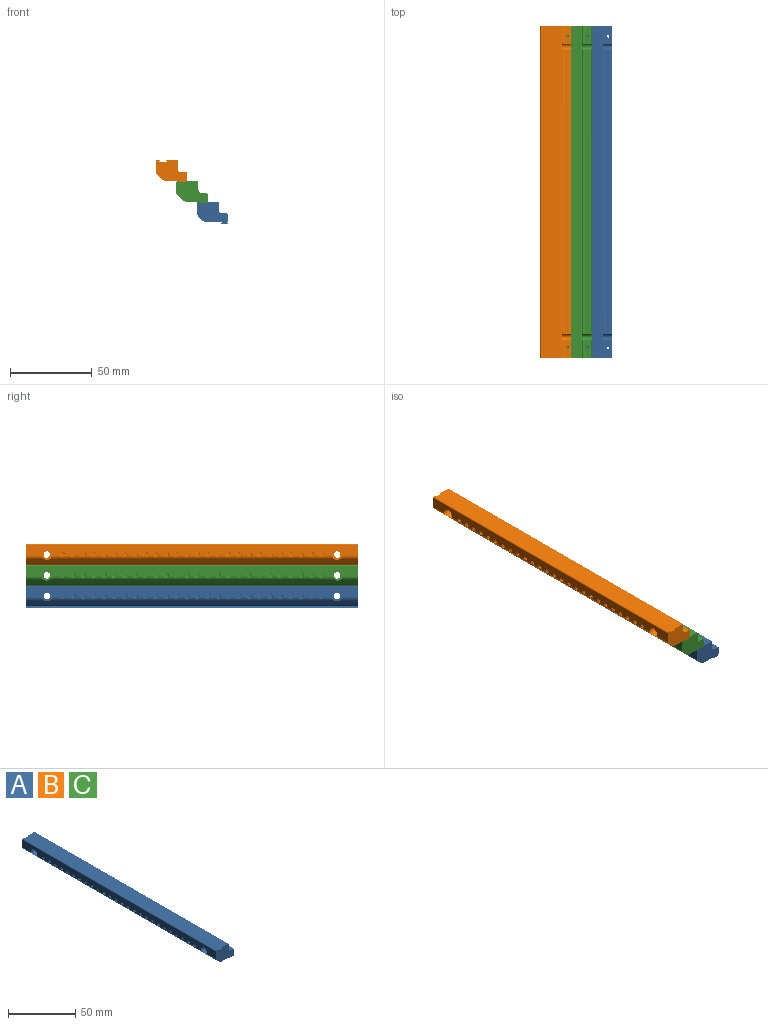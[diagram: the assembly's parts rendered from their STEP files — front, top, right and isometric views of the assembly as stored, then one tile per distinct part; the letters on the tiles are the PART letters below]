
ASSEMBLY  parts=3 mates=2
PART A: 227 faces, bbox 19.7x203.4x14 mm
  f0: cylinder r=3.17mm len=174.07mm, axis (0,-1,0), area 346.1mm2, adj f2,f39,f67,f69,f73,f74,f75,f79
  f1: plane 3.26x3.25mm, normal (-1,0,0), area 7.3mm2, adj f221,f222,f223,f226
  f2: plane 203.42x7.57mm, normal (-1,0,0), area 1082.2mm2, adj f0,f28,f38,f56,f57,f58,f67,f69
  f3: plane 3.26x3.25mm, normal (-1,0,0), area 7.3mm2, adj f215,f216,f217,f220
  f4: plane 3.26x3.25mm, normal (-1,0,0), area 7.3mm2, adj f209,f210,f211,f214
  f5: plane 3.26x3.25mm, normal (-1,0,0), area 7.3mm2, adj f203,f204,f205,f208
  f6: plane 3.26x3.25mm, normal (-1,0,0), area 7.3mm2, adj f197,f198,f199,f202
  f7: plane 3.26x3.25mm, normal (-1,0,0), area 7.3mm2, adj f191,f192,f193,f196
  f8: plane 3.26x3.25mm, normal (-1,0,0), area 7.3mm2, adj f185,f186,f187,f190
  f9: plane 3.26x3.25mm, normal (-1,0,0), area 7.3mm2, adj f179,f180,f181,f184
  f10: plane 3.26x3.25mm, normal (-1,0,0), area 7.3mm2, adj f173,f174,f175,f178
  f11: plane 3.26x3.25mm, normal (-1,0,0), area 7.3mm2, adj f167,f168,f169,f172
  f12: plane 3.26x3.25mm, normal (-1,0,0), area 7.3mm2, adj f161,f162,f163,f166
  f13: plane 3.26x3.25mm, normal (-1,0,0), area 7.3mm2, adj f155,f156,f157,f160
  f14: plane 3.26x3.25mm, normal (-1,0,0), area 7.3mm2, adj f149,f150,f151,f154
  f15: plane 3.26x3.25mm, normal (-1,0,0), area 7.3mm2, adj f143,f144,f145,f148
  f16: plane 3.26x3.25mm, normal (-1,0,0), area 7.3mm2, adj f137,f138,f139,f142
  f17: plane 3.26x3.25mm, normal (-1,0,0), area 7.3mm2, adj f131,f132,f133,f136
  f18: plane 3.26x3.25mm, normal (-1,0,0), area 7.3mm2, adj f125,f126,f127,f130
  f19: plane 3.26x3.25mm, normal (-1,0,0), area 7.3mm2, adj f119,f120,f121,f124
  f20: plane 3.26x3.25mm, normal (-1,0,0), area 7.3mm2, adj f113,f114,f115,f118
  f21: plane 3.26x3.25mm, normal (-1,0,0), area 7.3mm2, adj f107,f108,f109,f112
  f22: plane 3.26x3.25mm, normal (-1,0,0), area 7.3mm2, adj f101,f102,f103,f106
  f23: plane 3.26x3.25mm, normal (-1,0,0), area 7.3mm2, adj f95,f96,f97,f100
  f24: plane 3.26x3.25mm, normal (-1,0,0), area 7.3mm2, adj f89,f90,f91,f94
  f25: plane 3.26x3.25mm, normal (-1,0,0), area 7.3mm2, adj f83,f84,f85,f88
  f26: plane 3.26x3.25mm, normal (-1,0,0), area 7.3mm2, adj f77,f78,f79,f82
  f27: plane 3.26x3.25mm, normal (-1,0,0), area 7.3mm2, adj f71,f72,f73,f76
  f28: cylinder r=3.17mm len=10.84mm, axis (0,-1,0), area 24.9mm2, adj f2,f39,f58,f69
  f29: cylinder r=2.02mm len=14.22mm, axis (-1,0,0), area 136.6mm2, adj f31,f32,f33,f34,f35,f36,f46,f49
  f30: cylinder r=2.02mm len=14.22mm, axis (-1,0,0), area 136.6mm2, adj f31,f33,f35,f37,f46,f47,f48,f49
  f31: plane 174.12x3.18mm, normal (0,0,1), area 552.8mm2, adj f29,f30,f33,f35
  f32: plane 11x3.32mm, normal (0,0,1), area 32.1mm2, adj f29,f34,f36,f58,f63,f64,f65,f66
  f33: cylinder r=0.79mm len=175.39mm, axis (0,-1,0), area 217.6mm2, adj f29,f30,f31,f46
  f34: cylinder r=0.79mm len=11.5mm, axis (0,-1,0), area 13.8mm2, adj f29,f32,f46,f58
  f35: cylinder r=1.59mm len=174.12mm, axis (0,-1,0), area 434.1mm2, adj f29,f30,f31,f49
  f36: cylinder r=1.59mm len=10.86mm, axis (0,-1,0), area 27mm2, adj f29,f32,f49,f58
  f37: plane 11x3.32mm, normal (0,0,1), area 32.1mm2, adj f30,f47,f48,f57,f59,f60,f61,f62
  f38: cylinder r=3.17mm len=10.84mm, axis (0,-1,0), area 24.9mm2, adj f2,f39,f57,f67
  f39: plane 203.2x2.71mm, normal (-0.7,0,-0.71), area 771.8mm2, adj f0,f28,f38,f40,f57,f58,f67,f69
  f40: cylinder r=3.17mm len=203.2mm, axis (0,-1,0), area 504.1mm2, adj f39,f41,f57,f58
  f41: plane 203.2x9.24mm, normal (0,0,-1), area 1878.3mm2, adj f40,f42,f57,f58
  f42: plane 203.2x0.84mm, normal (-0.71,0,0.71), area 241.9mm2, adj f41,f43,f57,f58
  f43: plane 203.34x4.91mm, normal (0,0,-1), area 963mm2, adj f42,f44,f57,f58,f59,f60,f61,f62
  f44: plane 203.2x0.84mm, normal (0.71,0,0.71), area 241.9mm2, adj f43,f45,f57,f58
  f45: plane 203.2x0.84mm, normal (0,0,-1), area 171.1mm2, adj f44,f46,f57,f58
  f46: plane 203.2x4.71mm, normal (1,0,0), area 956.7mm2, adj f29,f30,f33,f34,f45,f47,f57,f58
  f47: cylinder r=0.79mm len=11.5mm, axis (0,-1,0), area 13.8mm2, adj f30,f37,f46,f57
  f48: cylinder r=1.59mm len=10.86mm, axis (0,-1,0), area 27mm2, adj f30,f37,f49,f57
  f49: plane 203.2x4.81mm, normal (1,0,0), area 970.7mm2, adj f29,f30,f35,f36,f48,f50,f57,f58
  f50: cylinder r=0.79mm len=203.2mm, axis (0,-1,0), area 253.4mm2, adj f49,f51,f57,f58
  f51: plane 203.2x7.01mm, normal (0,0,1), area 1424mm2, adj f50,f52,f57,f58
  f52: plane 203.2x0.84mm, normal (-0.71,0,-0.71), area 241.9mm2, adj f51,f53,f57,f58
  f53: plane 203.2x4.76mm, normal (0,0,1), area 967.7mm2, adj f52,f54,f57,f58
  f54: plane 203.2x0.84mm, normal (0.71,0,-0.71), area 241.9mm2, adj f53,f55,f57,f58
  f55: plane 203.2x1.82mm, normal (0,0,1), area 369.8mm2, adj f54,f56,f57,f58
  f56: cylinder r=0.79mm len=203.2mm, axis (0,-1,0), area 253.4mm2, adj f2,f55,f57,f58
  f57: plane 19.05x13.54mm, normal (0,1,0), area 191.3mm2, adj f2,f37,f38,f39,f40,f41,f42,f43
  f58: plane 19.05x13.54mm, normal (0,-1,0), area 191.3mm2, adj f2,f28,f32,f34,f36,f39,f40,f41
  f59: bspline ~6.78x2.35mm, area 22mm2, adj f37,f43,f61,f62
  f60: bspline ~6.78x2.35mm, area 21.9mm2, adj f37,f43,f61,f62
  f61: bspline ~6.59x2.41mm, area 6mm2, adj f37,f43,f59,f60
  f62: cylinder r=0.73mm len=6.35mm, axis (0,0,1), area 5.1mm2, adj f37,f43,f59,f60
  f63: bspline ~6.78x2.35mm, area 22mm2, adj f32,f43,f65,f66
  f64: bspline ~6.78x2.35mm, area 21.9mm2, adj f32,f43,f65,f66
  f65: bspline ~6.59x2.41mm, area 6mm2, adj f32,f43,f63,f64
  f66: cylinder r=0.73mm len=6.35mm, axis (0,0,1), area 5.1mm2, adj f32,f43,f63,f64
  f67: cylinder r=3.3mm len=6.6mm, axis (-1,0,0), area 93mm2, adj f0,f2,f38,f39,f68
  f68: plane 6.6x6.6mm, normal (-1,0,0), area 21.4mm2, adj f30,f67
  f69: cylinder r=3.3mm len=6.6mm, axis (-1,0,0), area 93mm2, adj f0,f2,f28,f39,f70
  f70: plane 6.6x6.6mm, normal (-1,0,0), area 21.4mm2, adj f29,f69
  f71: bspline ~10.17x4.06mm, area 58.1mm2, adj f2,f27,f73,f76
  f72: bspline ~10.17x4.06mm, area 57.8mm2, adj f2,f27,f73,f76
  f73: bspline ~9.89x4.15mm, area 15.3mm2, adj f0,f2,f27,f71,f72,f74,f75
  f74: cylinder r=1.78mm len=2.56mm, axis (-1,0,0), area 0mm2, adj f0,f2,f73
  f75: cylinder r=1.78mm len=2.63mm, axis (-1,0,0), area 0.2mm2, adj f0,f2,f73
  f76: cylinder r=1.33mm len=9.53mm, axis (-1,0,0), area 13.8mm2, adj f2,f27,f71,f72
  f77: bspline ~10.17x4.06mm, area 58.1mm2, adj f2,f26,f79,f82
  f78: bspline ~10.17x4.06mm, area 57.8mm2, adj f2,f26,f79,f82
  f79: bspline ~9.89x4.15mm, area 15.3mm2, adj f0,f2,f26,f77,f78,f80,f81
  f80: cylinder r=1.78mm len=2.56mm, axis (-1,0,0), area 0mm2, adj f0,f2,f79
  f81: cylinder r=1.78mm len=2.63mm, axis (-1,0,0), area 0.2mm2, adj f0,f2,f79
  f82: cylinder r=1.33mm len=9.53mm, axis (-1,0,0), area 13.8mm2, adj f2,f26,f77,f78
  f83: bspline ~10.17x4.06mm, area 58.1mm2, adj f2,f25,f85,f88
  f84: bspline ~10.17x4.06mm, area 57.8mm2, adj f2,f25,f85,f88
  f85: bspline ~9.89x4.15mm, area 15.3mm2, adj f0,f2,f25,f83,f84,f86,f87
  f86: cylinder r=1.78mm len=2.56mm, axis (-1,0,0), area 0mm2, adj f0,f2,f85
  f87: cylinder r=1.78mm len=2.63mm, axis (-1,0,0), area 0.2mm2, adj f0,f2,f85
  f88: cylinder r=1.33mm len=9.53mm, axis (-1,0,0), area 13.8mm2, adj f2,f25,f83,f84
  f89: bspline ~10.17x4.06mm, area 58.1mm2, adj f2,f24,f91,f94
  f90: bspline ~10.17x4.06mm, area 57.8mm2, adj f2,f24,f91,f94
  f91: bspline ~9.89x4.15mm, area 15.3mm2, adj f0,f2,f24,f89,f90,f92,f93
  f92: cylinder r=1.78mm len=2.56mm, axis (-1,0,0), area 0mm2, adj f0,f2,f91
  f93: cylinder r=1.78mm len=2.63mm, axis (-1,0,0), area 0.2mm2, adj f0,f2,f91
  f94: cylinder r=1.33mm len=9.53mm, axis (-1,0,0), area 13.8mm2, adj f2,f24,f89,f90
  f95: bspline ~10.17x4.06mm, area 58.1mm2, adj f2,f23,f97,f100
  f96: bspline ~10.17x4.06mm, area 57.8mm2, adj f2,f23,f97,f100
  f97: bspline ~9.89x4.15mm, area 15.3mm2, adj f0,f2,f23,f95,f96,f98,f99
  f98: cylinder r=1.78mm len=2.56mm, axis (-1,0,0), area 0mm2, adj f0,f2,f97
  f99: cylinder r=1.78mm len=2.63mm, axis (-1,0,0), area 0.2mm2, adj f0,f2,f97
  f100: cylinder r=1.33mm len=9.53mm, axis (-1,0,0), area 13.8mm2, adj f2,f23,f95,f96
  f101: bspline ~10.17x4.06mm, area 58.1mm2, adj f2,f22,f103,f106
  f102: bspline ~10.17x4.06mm, area 57.8mm2, adj f2,f22,f103,f106
  f103: bspline ~9.89x4.15mm, area 15.3mm2, adj f0,f2,f22,f101,f102,f104,f105
  f104: cylinder r=1.78mm len=2.56mm, axis (-1,0,0), area 0mm2, adj f0,f2,f103
  f105: cylinder r=1.78mm len=2.63mm, axis (-1,0,0), area 0.2mm2, adj f0,f2,f103
  f106: cylinder r=1.33mm len=9.53mm, axis (-1,0,0), area 13.8mm2, adj f2,f22,f101,f102
  f107: bspline ~10.17x4.06mm, area 58.1mm2, adj f2,f21,f109,f112
  f108: bspline ~10.17x4.06mm, area 57.8mm2, adj f2,f21,f109,f112
  f109: bspline ~9.89x4.15mm, area 15.3mm2, adj f0,f2,f21,f107,f108,f110,f111
  f110: cylinder r=1.78mm len=2.56mm, axis (-1,0,0), area 0mm2, adj f0,f2,f109
  f111: cylinder r=1.78mm len=2.63mm, axis (-1,0,0), area 0.2mm2, adj f0,f2,f109
  f112: cylinder r=1.33mm len=9.53mm, axis (-1,0,0), area 13.8mm2, adj f2,f21,f107,f108
  f113: bspline ~10.17x4.06mm, area 58.1mm2, adj f2,f20,f115,f118
  f114: bspline ~10.17x4.06mm, area 57.8mm2, adj f2,f20,f115,f118
  f115: bspline ~9.89x4.15mm, area 15.3mm2, adj f0,f2,f20,f113,f114,f116,f117
  f116: cylinder r=1.78mm len=2.56mm, axis (-1,0,0), area 0mm2, adj f0,f2,f115
  f117: cylinder r=1.78mm len=2.63mm, axis (-1,0,0), area 0.2mm2, adj f0,f2,f115
  f118: cylinder r=1.33mm len=9.53mm, axis (-1,0,0), area 13.8mm2, adj f2,f20,f113,f114
  f119: bspline ~10.17x4.06mm, area 58.1mm2, adj f2,f19,f121,f124
  f120: bspline ~10.17x4.06mm, area 57.8mm2, adj f2,f19,f121,f124
  f121: bspline ~9.89x4.15mm, area 15.3mm2, adj f0,f2,f19,f119,f120,f122,f123
  f122: cylinder r=1.78mm len=2.56mm, axis (-1,0,0), area 0mm2, adj f0,f2,f121
  f123: cylinder r=1.78mm len=2.63mm, axis (-1,0,0), area 0.2mm2, adj f0,f2,f121
  f124: cylinder r=1.33mm len=9.53mm, axis (-1,0,0), area 13.8mm2, adj f2,f19,f119,f120
  f125: bspline ~10.17x4.06mm, area 58.1mm2, adj f2,f18,f127,f130
  f126: bspline ~10.17x4.06mm, area 57.8mm2, adj f2,f18,f127,f130
  f127: bspline ~9.89x4.15mm, area 15.3mm2, adj f0,f2,f18,f125,f126,f128,f129
  f128: cylinder r=1.78mm len=2.56mm, axis (-1,0,0), area 0mm2, adj f0,f2,f127
  f129: cylinder r=1.78mm len=2.63mm, axis (-1,0,0), area 0.2mm2, adj f0,f2,f127
  f130: cylinder r=1.33mm len=9.53mm, axis (-1,0,0), area 13.8mm2, adj f2,f18,f125,f126
  f131: bspline ~10.17x4.06mm, area 58.1mm2, adj f2,f17,f133,f136
  f132: bspline ~10.17x4.06mm, area 57.8mm2, adj f2,f17,f133,f136
  f133: bspline ~9.89x4.15mm, area 15.3mm2, adj f0,f2,f17,f131,f132,f134,f135
  f134: cylinder r=1.78mm len=2.56mm, axis (-1,0,0), area 0mm2, adj f0,f2,f133
  f135: cylinder r=1.78mm len=2.63mm, axis (-1,0,0), area 0.2mm2, adj f0,f2,f133
  f136: cylinder r=1.33mm len=9.53mm, axis (-1,0,0), area 13.8mm2, adj f2,f17,f131,f132
  f137: bspline ~10.17x4.06mm, area 58.1mm2, adj f2,f16,f139,f142
  f138: bspline ~10.17x4.06mm, area 57.8mm2, adj f2,f16,f139,f142
  f139: bspline ~9.89x4.15mm, area 15.3mm2, adj f0,f2,f16,f137,f138,f140,f141
  f140: cylinder r=1.78mm len=2.56mm, axis (-1,0,0), area 0mm2, adj f0,f2,f139
  f141: cylinder r=1.78mm len=2.63mm, axis (-1,0,0), area 0.2mm2, adj f0,f2,f139
  f142: cylinder r=1.33mm len=9.53mm, axis (-1,0,0), area 13.8mm2, adj f2,f16,f137,f138
  f143: bspline ~10.17x4.06mm, area 58.1mm2, adj f2,f15,f145,f148
  f144: bspline ~10.17x4.06mm, area 57.8mm2, adj f2,f15,f145,f148
  f145: bspline ~9.89x4.15mm, area 15.3mm2, adj f0,f2,f15,f143,f144,f146,f147
  f146: cylinder r=1.78mm len=2.56mm, axis (-1,0,0), area 0mm2, adj f0,f2,f145
  f147: cylinder r=1.78mm len=2.63mm, axis (-1,0,0), area 0.2mm2, adj f0,f2,f145
  f148: cylinder r=1.33mm len=9.53mm, axis (-1,0,0), area 13.8mm2, adj f2,f15,f143,f144
  f149: bspline ~10.17x4.06mm, area 58.1mm2, adj f2,f14,f151,f154
  f150: bspline ~10.17x4.06mm, area 57.8mm2, adj f2,f14,f151,f154
  f151: bspline ~9.89x4.15mm, area 15.3mm2, adj f0,f2,f14,f149,f150,f152,f153
  f152: cylinder r=1.78mm len=2.56mm, axis (-1,0,0), area 0mm2, adj f0,f2,f151
  f153: cylinder r=1.78mm len=2.63mm, axis (-1,0,0), area 0.2mm2, adj f0,f2,f151
  f154: cylinder r=1.33mm len=9.53mm, axis (-1,0,0), area 13.8mm2, adj f2,f14,f149,f150
  f155: bspline ~10.17x4.06mm, area 58.1mm2, adj f2,f13,f157,f160
  f156: bspline ~10.17x4.06mm, area 57.8mm2, adj f2,f13,f157,f160
  f157: bspline ~9.89x4.15mm, area 15.3mm2, adj f0,f2,f13,f155,f156,f158,f159
  f158: cylinder r=1.78mm len=2.56mm, axis (-1,0,0), area 0mm2, adj f0,f2,f157
  f159: cylinder r=1.78mm len=2.63mm, axis (-1,0,0), area 0.2mm2, adj f0,f2,f157
  f160: cylinder r=1.33mm len=9.53mm, axis (-1,0,0), area 13.8mm2, adj f2,f13,f155,f156
  f161: bspline ~10.17x4.06mm, area 58.1mm2, adj f2,f12,f163,f166
  f162: bspline ~10.17x4.06mm, area 57.8mm2, adj f2,f12,f163,f166
  f163: bspline ~9.89x4.15mm, area 15.3mm2, adj f0,f2,f12,f161,f162,f164,f165
  f164: cylinder r=1.78mm len=2.56mm, axis (-1,0,0), area 0mm2, adj f0,f2,f163
  f165: cylinder r=1.78mm len=2.63mm, axis (-1,0,0), area 0.2mm2, adj f0,f2,f163
  f166: cylinder r=1.33mm len=9.53mm, axis (-1,0,0), area 13.8mm2, adj f2,f12,f161,f162
  f167: bspline ~10.17x4.06mm, area 58.1mm2, adj f2,f11,f169,f172
  f168: bspline ~10.17x4.06mm, area 57.8mm2, adj f2,f11,f169,f172
  f169: bspline ~9.89x4.15mm, area 15.3mm2, adj f0,f2,f11,f167,f168,f170,f171
  f170: cylinder r=1.78mm len=2.56mm, axis (-1,0,0), area 0mm2, adj f0,f2,f169
  f171: cylinder r=1.78mm len=2.63mm, axis (-1,0,0), area 0.2mm2, adj f0,f2,f169
  f172: cylinder r=1.33mm len=9.53mm, axis (-1,0,0), area 13.8mm2, adj f2,f11,f167,f168
  f173: bspline ~10.17x4.06mm, area 58.1mm2, adj f2,f10,f175,f178
  f174: bspline ~10.17x4.06mm, area 57.8mm2, adj f2,f10,f175,f178
  f175: bspline ~9.89x4.15mm, area 15.3mm2, adj f0,f2,f10,f173,f174,f176,f177
  f176: cylinder r=1.78mm len=2.56mm, axis (-1,0,0), area 0mm2, adj f0,f2,f175
  f177: cylinder r=1.78mm len=2.63mm, axis (-1,0,0), area 0.2mm2, adj f0,f2,f175
  f178: cylinder r=1.33mm len=9.53mm, axis (-1,0,0), area 13.8mm2, adj f2,f10,f173,f174
  f179: bspline ~10.17x4.06mm, area 58.1mm2, adj f2,f9,f181,f184
  f180: bspline ~10.17x4.06mm, area 57.8mm2, adj f2,f9,f181,f184
  f181: bspline ~9.89x4.15mm, area 15.3mm2, adj f0,f2,f9,f179,f180,f182,f183
  f182: cylinder r=1.78mm len=2.56mm, axis (-1,0,0), area 0mm2, adj f0,f2,f181
  f183: cylinder r=1.78mm len=2.63mm, axis (-1,0,0), area 0.2mm2, adj f0,f2,f181
  f184: cylinder r=1.33mm len=9.53mm, axis (-1,0,0), area 13.8mm2, adj f2,f9,f179,f180
  f185: bspline ~10.17x4.06mm, area 58.1mm2, adj f2,f8,f187,f190
  f186: bspline ~10.17x4.06mm, area 57.8mm2, adj f2,f8,f187,f190
  f187: bspline ~9.89x4.15mm, area 15.3mm2, adj f0,f2,f8,f185,f186,f188,f189
  f188: cylinder r=1.78mm len=2.56mm, axis (-1,0,0), area 0mm2, adj f0,f2,f187
  f189: cylinder r=1.78mm len=2.63mm, axis (-1,0,0), area 0.2mm2, adj f0,f2,f187
  f190: cylinder r=1.33mm len=9.53mm, axis (-1,0,0), area 13.8mm2, adj f2,f8,f185,f186
  f191: bspline ~10.17x4.06mm, area 58.1mm2, adj f2,f7,f193,f196
  f192: bspline ~10.17x4.06mm, area 57.8mm2, adj f2,f7,f193,f196
  f193: bspline ~9.89x4.15mm, area 15.3mm2, adj f0,f2,f7,f191,f192,f194,f195
  f194: cylinder r=1.78mm len=2.56mm, axis (-1,0,0), area 0mm2, adj f0,f2,f193
  f195: cylinder r=1.78mm len=2.63mm, axis (-1,0,0), area 0.2mm2, adj f0,f2,f193
  f196: cylinder r=1.33mm len=9.53mm, axis (-1,0,0), area 13.8mm2, adj f2,f7,f191,f192
  f197: bspline ~10.17x4.06mm, area 58.1mm2, adj f2,f6,f199,f202
  f198: bspline ~10.17x4.06mm, area 57.8mm2, adj f2,f6,f199,f202
  f199: bspline ~9.89x4.15mm, area 15.3mm2, adj f0,f2,f6,f197,f198,f200,f201
  f200: cylinder r=1.78mm len=2.56mm, axis (-1,0,0), area 0mm2, adj f0,f2,f199
  f201: cylinder r=1.78mm len=2.63mm, axis (-1,0,0), area 0.2mm2, adj f0,f2,f199
  f202: cylinder r=1.33mm len=9.53mm, axis (-1,0,0), area 13.8mm2, adj f2,f6,f197,f198
  f203: bspline ~10.17x4.06mm, area 58.1mm2, adj f2,f5,f205,f208
  f204: bspline ~10.17x4.06mm, area 57.8mm2, adj f2,f5,f205,f208
  f205: bspline ~9.89x4.15mm, area 15.3mm2, adj f0,f2,f5,f203,f204,f206,f207
  f206: cylinder r=1.78mm len=2.56mm, axis (-1,0,0), area 0mm2, adj f0,f2,f205
  f207: cylinder r=1.78mm len=2.63mm, axis (-1,0,0), area 0.2mm2, adj f0,f2,f205
  f208: cylinder r=1.33mm len=9.53mm, axis (-1,0,0), area 13.8mm2, adj f2,f5,f203,f204
  f209: bspline ~10.17x4.06mm, area 58.1mm2, adj f2,f4,f211,f214
  f210: bspline ~10.17x4.06mm, area 57.8mm2, adj f2,f4,f211,f214
  f211: bspline ~9.89x4.15mm, area 15.3mm2, adj f0,f2,f4,f209,f210,f212,f213
  f212: cylinder r=1.78mm len=2.56mm, axis (-1,0,0), area 0mm2, adj f0,f2,f211
  f213: cylinder r=1.78mm len=2.63mm, axis (-1,0,0), area 0.2mm2, adj f0,f2,f211
  f214: cylinder r=1.33mm len=9.53mm, axis (-1,0,0), area 13.8mm2, adj f2,f4,f209,f210
  f215: bspline ~10.17x4.06mm, area 58.1mm2, adj f2,f3,f217,f220
  f216: bspline ~10.17x4.06mm, area 57.8mm2, adj f2,f3,f217,f220
  f217: bspline ~9.89x4.15mm, area 15.3mm2, adj f0,f2,f3,f215,f216,f218,f219
  f218: cylinder r=1.78mm len=2.56mm, axis (-1,0,0), area 0mm2, adj f0,f2,f217
  f219: cylinder r=1.78mm len=2.63mm, axis (-1,0,0), area 0.2mm2, adj f0,f2,f217
  f220: cylinder r=1.33mm len=9.53mm, axis (-1,0,0), area 13.8mm2, adj f2,f3,f215,f216
  f221: bspline ~10.17x4.06mm, area 58.1mm2, adj f1,f2,f223,f226
  f222: bspline ~10.17x4.06mm, area 57.8mm2, adj f1,f2,f223,f226
  f223: bspline ~9.89x4.15mm, area 15.3mm2, adj f0,f1,f2,f221,f222,f224,f225
  f224: cylinder r=1.78mm len=2.56mm, axis (-1,0,0), area 0mm2, adj f0,f2,f223
  f225: cylinder r=1.78mm len=2.63mm, axis (-1,0,0), area 0.2mm2, adj f0,f2,f223
  f226: cylinder r=1.33mm len=9.53mm, axis (-1,0,0), area 13.8mm2, adj f1,f2,f221,f222
PART B: same geometry as A
PART C: same geometry as A
PLACE A t=(37.17,-52.23,20.62)mm
PLACE B t=(12.14,-52.23,46.02)mm
PLACE C t=(24.66,-52.23,33.32)mm
MATE fastened C.f44 <-> A.f52  axis (0.71,0,0.71) through (54.07,-52.23,30.57)mm
MATE fastened B.f44 <-> C.f52  axis (0.71,0,0.71) through (41.55,-52.23,43.27)mm
